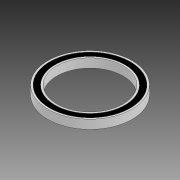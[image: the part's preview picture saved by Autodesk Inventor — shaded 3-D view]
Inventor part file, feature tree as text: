
AUTODESK INVENTOR PART (.ipt)
format: ipt  version: 2022 (Build 260153000, 153)  size: 131,072 bytes
history: native  units: mm
features: revolve x1, sketch x1
ambient origin geometry x8: Origin, YZ Plane, XZ Plane, XY Plane, X Axis, Y Axis, Z Axis, Center Point
bodies: Solid1 (feature_tree)
feature tree (2):
  revolve  "Revolution1"  [1 undecoded]
  sketch  "Sketch1"  dims[d0=37.5mm d2=10.0mm d5=47.5mm d6=0.2mm d7=2.0mm d8=90.0deg]
note: 1 required parameter value undecoded (feature->parameter linkage not recoverable at this tier; creation-order binding heuristic only, values carry confidence <= 0.55)
